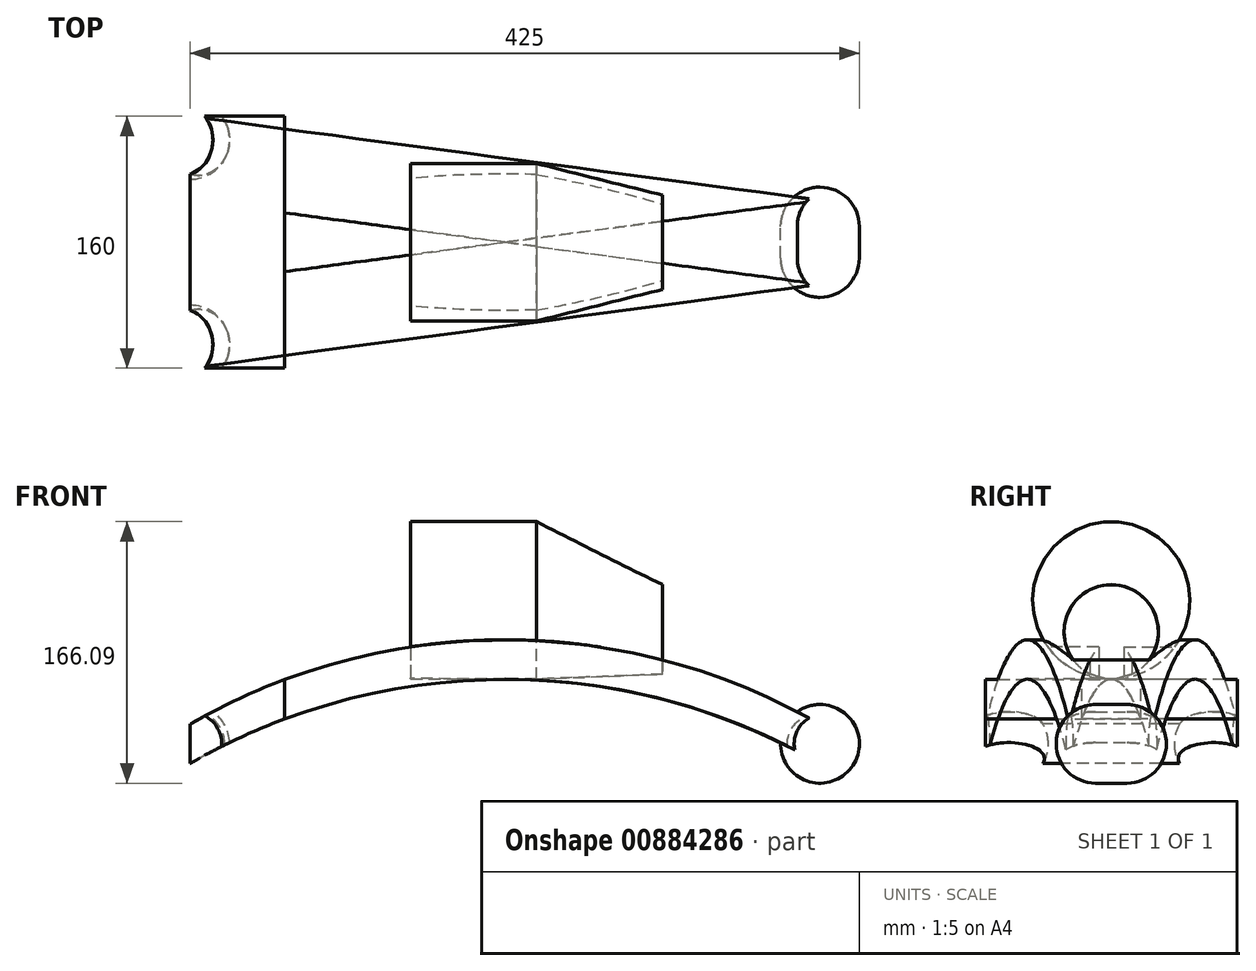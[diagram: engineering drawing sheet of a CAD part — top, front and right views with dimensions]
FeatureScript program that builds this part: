
annotation { "Feature Type Name" : "Feature", "Feature Type Description" : "" }
export const myFeature = defineFeature(function(context is Context, id is Id, definition is map)
    precondition{}
    {
        {
            var Q0;
            Q0=qCreatedBy(makeId("Front.planeOp"),FACE);
            var sketch = newSketch(context, id + "F0", { "sketchPlane" : qUnion([Q0])});
            skLineSegment(sketch, "E0", {"start": v(-200, -12.5) * mm, "end": v(-200, 12.5) * mm});
            skArc(sketch, "E1", {"start": v(-200, 12.5) * mm, "mid": v(0, 66.09) * mm, "end": v(200, 12.5) * mm});
            skLineSegment(sketch, "E2", {"start": v(200, 12.5) * mm, "end": v(200, -12.5) * mm});
            skArc(sketch, "E3", {"start": v(-200, -12.5) * mm, "mid": v(0, 41.09) * mm, "end": v(200, -12.5) * mm});
            skPoint(sketch, "E4", {"position": v(-200, 0) * mm});
            skPoint(sketch, "E5", {"position": v(0, 66.09) * mm});
            skSolve(sketch);
        }
        {
            var Q0;
            Q0=makeQuery(id+"F0.imprint","IMPRINT",FACE,{"disambiguationData":[TD([[makeQuery(id+"F0.imprint","IMPRINT",EDGE,{"derivedFrom":sQuery(id+"F0.wireOp",EDGE,"E0")}),-1.0]])]});
            extrude(context, id + "F1", {"entities" : qUnion([Q0]), "endBound" : BoundingType.SYMMETRIC, "depth" : 160 * mm, "offsetDistance" : 25 * mm});
        }
        {
            var Q0;
            Q0=qCreatedBy(makeId("Top.planeOp"),FACE);
            var sketch = newSketch(context, id + "F2", { "sketchPlane" : qUnion([Q0])});
            skLineSegment(sketch, "E6", {"start": v(-200, -80) * mm, "end": v(-200, 80) * mm});
            skLineSegment(sketch, "E7", {"start": v(-200, 80) * mm, "end": v(200, 26.67) * mm});
            skLineSegment(sketch, "E8", {"start": v(200, 26.67) * mm, "end": v(200, -26.67) * mm});
            skLineSegment(sketch, "E9", {"start": v(200, -26.67) * mm, "end": v(-140, 18.67) * mm});
            skLineSegment(sketch, "E10", {"start": v(-140, 18.67) * mm, "end": v(-140, -80) * mm});
            skLineSegment(sketch, "E11", {"start": v(-140, -80) * mm, "end": v(-200, -80) * mm});
            skPoint(sketch, "E12", {"position": v(-200, 0) * mm});
            skLineSegment(sketch, "E13", {"start": v(-200, 80) * mm, "end": v(200, 80) * mm});
            skLineSegment(sketch, "E14", {"start": v(200, 80) * mm, "end": v(200, 26.67) * mm});
            skLineSegment(sketch, "E15", {"start": v(-140, -80) * mm, "end": v(200, -80) * mm});
            skLineSegment(sketch, "E16", {"start": v(200, -80) * mm, "end": v(200, -26.67) * mm});
            skPoint(sketch, "E17", {"position": v(200, 0) * mm});
            skSolve(sketch);
        }
        {
            var Q0;
            Q0=makeQuery(id+"F2.imprint","IMPRINT",FACE,{"disambiguationData":[TD([[makeQuery(id+"F2.imprint","IMPRINT",EDGE,{"derivedFrom":sQuery(id+"F2.wireOp",EDGE,"E9")}),1.0]])]});
            var Q1;
            Q1=makeQuery(id+"F2.imprint","IMPRINT",FACE,{"disambiguationData":[TD([[makeQuery(id+"F2.imprint","IMPRINT",EDGE,{"derivedFrom":sQuery(id+"F2.wireOp",EDGE,"E7")}),1.0]])]});
            extrude(context, id + "F3", {"entities" : qUnion([Q0, Q1]), "operationType" : NewBodyOperationType.REMOVE, "endBound" : BoundingType.THROUGH_ALL, "oppositeDirection" : true, "depth" : 25 * mm, "offsetDistance" : 25 * mm, "hasSecondDirection" : true, "secondDirectionBound" : SecondDirectionBoundingType.THROUGH_ALL, "secondDirectionOppositeDirection" : false, "secondDirectionDepth" : 25 * mm});
        }
        {
            var Q0;
            Q0=makeQuery(id+"F1.opExtrude","SWEPT_FACE",FACE,{"disambiguationData":[OSD([sQuery(id+"F0.wireOp",EDGE,"E0")])]});
            var sketch = newSketch(context, id + "F4", { "sketchPlane" : qUnion([Q0])});
            skArc(sketch, "E18", {"start": v(-90, 0) * mm, "mid": v(-65, 25) * mm, "end": v(-40, 0) * mm});
            skArc(sketch, "E19", {"start": v(40, 0) * mm, "mid": v(65, 25) * mm, "end": v(90, 0) * mm});
            skLineSegment(sketch, "E20", {"start": v(-90, 0) * mm, "end": v(-40, 0) * mm});
            skLineSegment(sketch, "E21", {"start": v(40, 0) * mm, "end": v(90, 0) * mm});
            skSolve(sketch);
        }
        {
            var Q0;
            Q0=qSketchRegion(id+"F4",true);
            var Q1;
            Q1=sQuery(id+"F4.wireOp",EDGE,"E20");
            revolve(context, id + "F5", {"operationType" : NewBodyOperationType.ADD, "surfaceOperationType" : NewSurfaceOperationType.NEW, "entities" : qUnion([Q0]), "axis" : qUnion([Q1]), "revolveType" : RevolveType.FULL});
        }
        {
            var Q0;
            Q0=makeQuery(id+"F1.opExtrude","SWEPT_FACE",FACE,{"disambiguationData":[OSD([sQuery(id+"F0.wireOp",EDGE,"E2")])]});
            var sketch = newSketch(context, id + "F6", { "sketchPlane" : qUnion([Q0])});
            skLineSegment(sketch, "E22", {"start": v(-10, 25) * mm, "end": v(10, 25) * mm});
            skArc(sketch, "E23", {"start": v(-35, 0) * mm, "mid": v(-27.68, 17.68) * mm, "end": v(-10, 25) * mm});
            skPoint(sketch, "E23.startSnap0", {"position": v(-26.67, 0) * mm});
            skArc(sketch, "E24", {"start": v(10, 25) * mm, "mid": v(27.68, 17.68) * mm, "end": v(35, 0) * mm});
            skLineSegment(sketch, "E25", {"start": v(-35, 0) * mm, "end": v(35, 0) * mm});
            skSolve(sketch);
        }
        {
            var Q0;
            Q0=qSketchRegion(id+"F6",true);
            var Q1;
            Q1=sQuery(id+"F6.wireOp",EDGE,"E25");
            revolve(context, id + "F7", {"operationType" : NewBodyOperationType.ADD, "surfaceOperationType" : NewSurfaceOperationType.NEW, "entities" : qUnion([Q0]), "axis" : qUnion([Q1]), "revolveType" : RevolveType.FULL});
        }
        {
            var Q0;
            Q0=qCreatedBy(makeId("Front.planeOp"),FACE);
            var sketch = newSketch(context, id + "F8", { "sketchPlane" : qUnion([Q0])});
            skLineSegment(sketch, "E26", {"start": v(20, 91.09) * mm, "end": v(-60, 91.09) * mm});
            skLineSegment(sketch, "E27", {"start": v(-60, 91.09) * mm, "end": v(-60, 141.09) * mm});
            skLineSegment(sketch, "E28", {"start": v(-60, 141.09) * mm, "end": v(20, 141.09) * mm});
            skLineSegment(sketch, "E29", {"start": v(20, 141.09) * mm, "end": v(20, 91.09) * mm});
            skSolve(sketch);
        }
        {
            var Q0;
            Q0=qSketchRegion(id+"F8",true);
            var Q1;
            Q1=sQuery(id+"F8.wireOp",EDGE,"E26");
            revolve(context, id + "F9", {"operationType" : NewBodyOperationType.ADD, "surfaceOperationType" : NewSurfaceOperationType.NEW, "entities" : qUnion([Q0]), "axis" : qUnion([Q1]), "revolveType" : RevolveType.FULL});
        }
        {
            var Q0;
            Q0=qCreatedBy(makeId("Right.planeOp"),FACE);
            cPlane(context, id + "F10", {"entities" : qUnion([Q0]), "cplaneType" : CPlaneType.OFFSET, "offset" : 100 * mm, "width" : 150 * mm, "height" : 150 * mm});
        }
        {
            var Q0;
            Q0=qCreatedBy(id+"F10.planeOp",FACE);
            var sketch = newSketch(context, id + "F11", { "sketchPlane" : qUnion([Q0])});
            skCircle(sketch, "E30", {"center": v(0, 71.09) * mm, "radius": 30 * mm});
            skPoint(sketch, "E31", {"position": v(30, 71.09) * mm});
            skPoint(sketch, "E32", {"position": v(-30, 71.09) * mm});
            skLineSegment(sketch, "E33", {"start": v(-13.33, 44.22) * mm, "end": v(-13.33, 53.39) * mm});
            skLineSegment(sketch, "E34", {"start": v(-13.33, 53.39) * mm, "end": v(24.22, 53.39) * mm});
            skSolve(sketch);
        }
        {
            var Q0;
            Q0=makeQuery(id+"F9.opRevolve","SWEPT_FACE",FACE,{"disambiguationData":[OSD([sQuery(id+"F8.wireOp",EDGE,"E29")])]});
            var sketch = newSketch(context, id + "F12", { "sketchPlane" : qUnion([Q0])});
            skPoint(sketch, "E35", {"position": v(0, 91.09) * mm});
            skPoint(sketch, "E36", {"position": v(50, 91.09) * mm});
            skPoint(sketch, "E37", {"position": v(-50, 91.09) * mm});
            skSolve(sketch);
        }
        {
            var Q1;
            {var subQ0=sQuery(id+"F8.wireOp",EDGE,"E29");Q1=makeQuery(id+"F12.imprint","IMPRINT",FACE,{"disambiguationData":[TD([[makeQuery(id+"F12.imprint","IMPRINT",EDGE,{"derivedFrom":makeQuery(id+"F9.opRevolve","SWEPT_EDGE",EDGE,{"disambiguationData":[OSD([sQuery(id+"F8.wireOp",EDGE,"E28"),subQ0])]})}),1.0]])]});}
            var Q2;
            {var subQ0=sQuery(id+"F11.wireOp",EDGE,"E33");Q2=makeQuery(id+"F11.imprint","IMPRINT",FACE,{"disambiguationData":[TD([[makeQuery(id+"F11.imprint","IMPRINT",EDGE,{"derivedFrom":subQ0}),1.0]])]});}
            loft(context, id + "F13", {"operationType" : NewBodyOperationType.ADD, "sheetProfilesArray" : [{ "sheetProfileEntities" : qUnion([Q1]) }, { "sheetProfileEntities" : qUnion([Q2]) }]});
        }
        {
            var Q0;
            Q0=makeQuery(id+"F1.opExtrude","SWEPT_BODY",BODY,{"disambiguationData":[OSD([sQuery(id+"F0.wireOp",EDGE,"E0"),sQuery(id+"F0.wireOp",EDGE,"E1"),sQuery(id+"F0.wireOp",EDGE,"E2"),sQuery(id+"F0.wireOp",EDGE,"E3")])]});
            var Q1;
            Q1=qCreatedBy(makeId("Front.planeOp"),FACE);
            mirror(context, id + "F14", {"entities" : qUnion([Q0]), "mirrorPlane" : qUnion([Q1])});
        }
    });
